FCSTD DOCUMENT
Label: CBGneck-headstockonly-25
objects: Sketcher::SketchObject×1
note: 1 computed .brp shape members not serialized (recipe doc carries the construction recipe); baked Part::Feature solids carry a one-line shape summary decoded from their .brp

FEATURE [Sketcher::SketchObject] Sketch  label="CBG-neck"
  Placement = pos=(0,0,0) rot=(1,0,0;1.5708rad)
  sketch-geometry (13):
    g0: LineSegment StartX=0 StartY=0 StartZ=0 EndX=901.7 EndY=0 EndZ=0
    g1: LineSegment StartX=901.7 StartY=0 StartZ=0 EndX=901.7 EndY=16 EndZ=0
    g2: LineSegment StartX=737.013 StartY=26.8 StartZ=0 EndX=737.013 EndY=19.8 EndZ=0
    g3: LineSegment StartX=737.013 StartY=19.8 StartZ=0 EndX=725.9 EndY=19.8 EndZ=0
    g4: LineSegment StartX=725.9 StartY=19.8 StartZ=0 EndX=725.9 EndY=26.8 EndZ=0
    g5: LineSegment StartX=725.9 StartY=26.8 StartZ=0 EndX=112.312 EndY=26.8 EndZ=0
    g6: LineSegment StartX=0 StartY=20 StartZ=0 EndX=0 EndY=0 EndZ=0
    g7: LineSegment StartX=742.013 StartY=26.8 StartZ=0 EndX=737.013 EndY=26.8 EndZ=0
    g8: LineSegment StartX=742.013 StartY=26.8 StartZ=0 EndX=747.013 EndY=21.8 EndZ=0
    g9: LineSegment StartX=747.013 StartY=21.8 StartZ=0 EndX=747.013 EndY=16 EndZ=0
    g10: LineSegment StartX=747.013 StartY=16 StartZ=0 EndX=901.7 EndY=16 EndZ=0
    g11: LineSegment StartX=112.312 StartY=26.8 StartZ=0 EndX=0 EndY=26.8 EndZ=0
    g12: LineSegment StartX=0 StartY=26.8 StartZ=0 EndX=0 EndY=20 EndZ=0
  constraints (34):
    c: Coincident(g0,g1)
    c: Vertical(g1)
    c: Coincident(g2,g3)
    c: Coincident(g3,g4)
    c: Coincident(g4,g5)
    c: Coincident(g6,g0)
    c: Vertical(g6)
    c: Coincident(g7,g2)
    c: Vertical(g2)
    c: Vertical(g4)
    c: DistanceX(g3) = -11.1125
    c: DistanceY(g1) = 16
    c: Horizontal(g0)
    c: Horizontal(g5)
    c: Horizontal(g3)
    c: Horizontal(g7)
    c: DistanceX(g7) = -5
    c: DistanceY(g4) = 7
    c: Equal(g4,g2)
    c: DistanceY(g0,g7) = 26.8
    c: DistanceY(g6,g0) = -20
    c: Coincident(g7,g8)
    c: Coincident(g8,g9)
    c: Vertical(g9)
    c: Coincident(g9,g10)
    c: Coincident(g10,g1)
    c: Horizontal(g10)
    c: DistanceX(g2,g9) = 10
    c: Angle(g7,g8) = 2.35619
    c: Coincident(g0,g-1)
    c: DistanceX(g0) = 901.7
    c: Horizontal(g11)
    c: Coincident(g11,g12)
    c: Vertical(g12)
